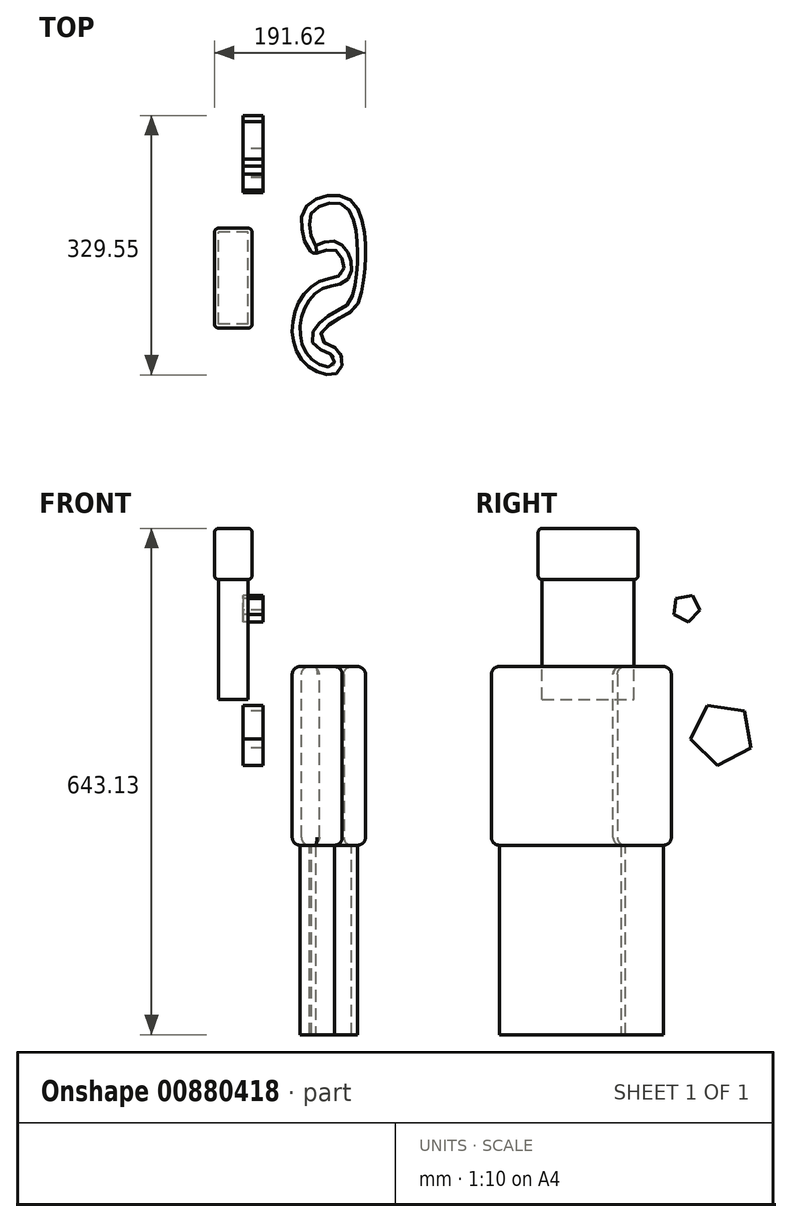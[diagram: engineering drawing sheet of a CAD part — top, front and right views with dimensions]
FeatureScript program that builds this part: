
annotation { "Feature Type Name" : "Feature", "Feature Type Description" : "" }
export const myFeature = defineFeature(function(context is Context, id is Id, definition is map)
    precondition{}
    {
        {
            var Q0;
            Q0=qCreatedBy(makeId("Front.planeOp"),FACE);
            var sketch = newSketch(context, id + "F0", { "sketchPlane" : qUnion([Q0])});
            skLineSegment(sketch, "E0.bottom", {"start": v(11.32, 23.07) * mm, "end": v(-36.3, 23.07) * mm});
            skLineSegment(sketch, "E0.top", {"start": v(11.32, -41.84) * mm, "end": v(-36.3, -41.84) * mm});
            skLineSegment(sketch, "E0.left", {"start": v(11.32, 23.07) * mm, "end": v(11.32, -41.84) * mm});
            skLineSegment(sketch, "E0.right", {"start": v(-36.3, 23.07) * mm, "end": v(-36.3, -41.84) * mm});
            skSolve(sketch);
        }
        {
            var Q0;
            Q0=qSketchRegion(id+"F0",true);
            var Q1;
            Q1=makeQuery(id+"F0.imprint","IMPRINT",FACE,{"disambiguationData":[TD([[makeQuery(id+"F0.imprint","IMPRINT",EDGE,{"derivedFrom":sQuery(id+"F0.wireOp",EDGE,"E0.bottom")}),1.0]])]});
            extrude(context, id + "F1", {"entities" : qUnion([Q0, Q1]), "depth" : 126.82 * mm, "offsetDistance" : 25 * mm});
        }
        {
            var Q0;
            Q0=makeQuery(id+"F1.opExtrude","SWEPT_FACE",FACE,{"disambiguationData":[OSD([sQuery(id+"F0.wireOp",EDGE,"E0.left")])]});
            var Q1;
            Q1=makeQuery(id+"F1.opExtrude","SWEPT_FACE",FACE,{"disambiguationData":[OSD([sQuery(id+"F0.wireOp",EDGE,"E0.right")])]});
            var Q2;
            Q2=makeQuery(id+"F1.opExtrude","CAP_FACE",FACE,{"disambiguationData":[OSD([sQuery(id+"F0.wireOp",EDGE,"E0.bottom"),sQuery(id+"F0.wireOp",EDGE,"E0.top"),sQuery(id+"F0.wireOp",EDGE,"E0.left"),sQuery(id+"F0.wireOp",EDGE,"E0.right")])],"isStart":false});
            var Q3;
            Q3=makeQuery(id+"F1.opExtrude","SWEPT_FACE",FACE,{"disambiguationData":[OSD([sQuery(id+"F0.wireOp",EDGE,"E0.bottom")])]});
            var Q4;
            Q4=makeQuery(id+"F1.opExtrude","SWEPT_FACE",FACE,{"disambiguationData":[OSD([sQuery(id+"F0.wireOp",EDGE,"E0.top")])]});
            fillet(context, id + "F2", {"entities" : qUnion([Q0, Q1, Q2, Q3, Q4]), "radius" : 5 * mm, "tangentPropagation" : true, "allowEdgeOverflow" : false});
        }
        {
            var Q0;
            Q0=makeQuery(id+"F1.opExtrude","SWEPT_FACE",FACE,{"disambiguationData":[OSD([sQuery(id+"F0.wireOp",EDGE,"E0.top")])]});
            extrude(context, id + "F3", {"entities" : qUnion([Q0]), "operationType" : NewBodyOperationType.ADD, "depth" : 110.6 * mm, "offsetDistance" : 25 * mm});
        }
        {
            var Q0;
            Q0=makeQuery(id+"F3.opExtrude","CAP_FACE",FACE,{"disambiguationData":[OSD([sQuery(id+"F0.wireOp",EDGE,"E0.top")])],"isStart":false});
            var sketch = newSketch(context, id + "F4", { "sketchPlane" : qUnion([Q0])});
            skSolve(sketch);
        }
        {
            var Q0;
            {var subQ0=sQuery(id+"F0.wireOp",EDGE,"E0.top");var subQ1=makeQuery(id+"F1.opExtrude","SWEPT_FACE",FACE,{"disambiguationData":[OSD([subQ0])]});Q0=makeQuery(id+"F4.imprint","IMPRINT",FACE,{"disambiguationData":[TD([[makeQuery(id+"F4.imprint","IMPRINT",EDGE,{"derivedFrom":makeQuery(id+"F3.opExtrude","CAP_EDGE",EDGE,{"disambiguationData":[OSD([subQ0]),TDD([makeQuery(id+"F2.opFillet","BLEND_EDGE",EDGE,{"blendedFrom":[makeQuery(id+"F1.opExtrude","CAP_EDGE",EDGE,{"disambiguationData":[OSD([subQ0])],"isStart":true}),subQ1],"blendedInto":[subQ1]})])],"isStart":false})}),1.0]])]});}
            var sketch = newSketch(context, id + "F5", { "sketchPlane" : qUnion([Q0])});
            skSolve(sketch);
        }
        {
            var Q0;
            {var subQ0=sQuery(id+"F0.wireOp",EDGE,"E0.top");var subQ1=makeQuery(id+"F1.opExtrude","SWEPT_FACE",FACE,{"disambiguationData":[OSD([subQ0])]});Q0=makeQuery(id+"F4.imprint","IMPRINT",FACE,{"disambiguationData":[TD([[makeQuery(id+"F4.imprint","IMPRINT",EDGE,{"derivedFrom":makeQuery(id+"F3.opExtrude","CAP_EDGE",EDGE,{"disambiguationData":[OSD([subQ0]),TDD([makeQuery(id+"F2.opFillet","BLEND_EDGE",EDGE,{"blendedFrom":[makeQuery(id+"F1.opExtrude","CAP_EDGE",EDGE,{"disambiguationData":[OSD([subQ0])],"isStart":true}),subQ1],"blendedInto":[subQ1]})])],"isStart":false})}),1.0]])]});}
            var sketch = newSketch(context, id + "F6", { "sketchPlane" : qUnion([Q0])});
            skSolve(sketch);
        }
        {
            var Q0;
            {var subQ0=sQuery(id+"F0.wireOp",EDGE,"E0.top");var subQ1=makeQuery(id+"F1.opExtrude","SWEPT_FACE",FACE,{"disambiguationData":[OSD([subQ0])]});Q0=makeQuery(id+"F6.imprint","IMPRINT",FACE,{"disambiguationData":[TD([[makeQuery(id+"F6.imprint","IMPRINT",EDGE,{"derivedFrom":makeQuery(id+"F4.imprint","IMPRINT",EDGE,{"derivedFrom":makeQuery(id+"F3.opExtrude","CAP_EDGE",EDGE,{"disambiguationData":[OSD([subQ0]),TDD([makeQuery(id+"F2.opFillet","BLEND_EDGE",EDGE,{"blendedFrom":[makeQuery(id+"F1.opExtrude","CAP_EDGE",EDGE,{"disambiguationData":[OSD([subQ0])],"isStart":true}),subQ1],"blendedInto":[subQ1]})])],"isStart":false})})}),1.0]])]});}
            var Q1;
            {var subQ0=sQuery(id+"F0.wireOp",EDGE,"E0.top");var subQ1=makeQuery(id+"F1.opExtrude","SWEPT_FACE",FACE,{"disambiguationData":[OSD([subQ0])]});Q1=makeQuery(id+"F4.imprint","IMPRINT",FACE,{"disambiguationData":[TD([[makeQuery(id+"F4.imprint","IMPRINT",EDGE,{"derivedFrom":makeQuery(id+"F3.opExtrude","CAP_EDGE",EDGE,{"disambiguationData":[OSD([subQ0]),TDD([makeQuery(id+"F2.opFillet","BLEND_EDGE",EDGE,{"blendedFrom":[makeQuery(id+"F1.opExtrude","CAP_EDGE",EDGE,{"disambiguationData":[OSD([subQ0])],"isStart":true}),subQ1],"blendedInto":[subQ1]})])],"isStart":false})}),1.0]])]});}
            extrude(context, id + "F7", {"entities" : qUnion([Q0, Q1]), "operationType" : NewBodyOperationType.ADD, "depth" : 41.48 * mm, "offsetDistance" : 25 * mm});
        }
        {
            var Q0;
            {var subQ0=sQuery(id+"F0.wireOp",EDGE,"E0.right");var subQ1=sQuery(id+"F0.wireOp",EDGE,"E0.top");Q0=makeQuery(id+"F7.boolean.opBoolean","MERGE",FACE,{"derivedFrom":[makeQuery(id+"F3.opExtrude","SWEPT_FACE",FACE,{"disambiguationData":[OSD([subQ1,subQ0])]}),makeQuery(id+"F7.opExtrude","SWEPT_FACE",FACE,{"disambiguationData":[OSD([subQ1,subQ0]),TDD([makeQuery(id+"F4.imprint","IMPRINT",EDGE,{"derivedFrom":makeQuery(id+"F3.opExtrude","CAP_EDGE",EDGE,{"disambiguationData":[OSD([subQ1,subQ0])],"isStart":false})})])]})]});}
            var sketch = newSketch(context, id + "F8", { "sketchPlane" : qUnion([Q0])});
            skSolve(sketch);
        }
        {
            var Q0;
            Q0=qCreatedBy(makeId("Right.planeOp"),FACE);
            var sketch = newSketch(context, id + "F9", { "sketchPlane" : qUnion([Q0])});
            skCircle(sketch, "E1.cCircle", {"center": v(61.13, -78.12) * mm, "radius": 17.9 * mm, "construction": true});
            skLineSegment(sketch, "E1.0", {"start": v(64.3, -95.74) * mm, "end": v(45.36, -86.58) * mm});
            skLineSegment(sketch, "E1.1", {"start": v(45.36, -86.58) * mm, "end": v(48.2, -65.73) * mm});
            skLineSegment(sketch, "E1.2", {"start": v(48.2, -65.73) * mm, "end": v(68.92, -62) * mm});
            skLineSegment(sketch, "E1.3", {"start": v(68.92, -62) * mm, "end": v(78.87, -80.54) * mm});
            skLineSegment(sketch, "E1.4", {"start": v(78.87, -80.54) * mm, "end": v(64.3, -95.74) * mm});
            skCircle(sketch, "E2.cCircle", {"center": v(106.86, -237.6) * mm, "radius": 40.61 * mm, "construction": true});
            skLineSegment(sketch, "E2.0", {"start": v(135.23, -208.54) * mm, "end": v(143.27, -255.6) * mm});
            skLineSegment(sketch, "E2.1", {"start": v(143.27, -255.6) * mm, "end": v(101, -277.8) * mm});
            skLineSegment(sketch, "E2.2", {"start": v(101, -277.8) * mm, "end": v(66.83, -244.45) * mm});
            skLineSegment(sketch, "E2.3", {"start": v(66.83, -244.45) * mm, "end": v(87.99, -201.65) * mm});
            skLineSegment(sketch, "E2.4", {"start": v(87.99, -201.65) * mm, "end": v(135.23, -208.54) * mm});
            skSolve(sketch);
        }
        {
            var Q0;
            Q0=makeQuery(id+"F9.imprint","IMPRINT",FACE,{"disambiguationData":[TD([[makeQuery(id+"F9.imprint","IMPRINT",EDGE,{"derivedFrom":sQuery(id+"F9.wireOp",EDGE,"E1.0")}),-1.0]])]});
            var Q1;
            Q1=makeQuery(id+"F9.imprint","IMPRINT",FACE,{"disambiguationData":[TD([[makeQuery(id+"F9.imprint","IMPRINT",EDGE,{"derivedFrom":sQuery(id+"F9.wireOp",EDGE,"E2.0")}),-1.0]])]});
            extrude(context, id + "F10", {"entities" : qUnion([Q0, Q1]), "depth" : 25 * mm, "offsetDistance" : 25 * mm});
        }
        {
            var Q0;
            {var subQ0=sQuery(id+"F0.wireOp",EDGE,"E0.right");var subQ1=sQuery(id+"F0.wireOp",EDGE,"E0.top");var subQ4=makeQuery(id+"F3.opExtrude","CAP_EDGE",EDGE,{"disambiguationData":[OSD([subQ1,subQ0])],"isStart":false});Q0=makeQuery(id+"F8.imprint","IMPRINT",FACE,{"disambiguationData":[TD([[makeQuery(id+"F8.imprint","IMPRINT",EDGE,{"derivedFrom":makeQuery(id+"F7.opExtrude","CAP_EDGE",EDGE,{"disambiguationData":[OSD([subQ1,subQ0]),TDD([makeQuery(id+"F4.imprint","IMPRINT",EDGE,{"derivedFrom":subQ4})])],"isStart":false})}),-1.0]])]});}
            var sketch = newSketch(context, id + "F11", { "sketchPlane" : qUnion([Q0])});
            skSolve(sketch);
        }
        {
            var Q0;
            {var subQ0=sQuery(id+"F0.wireOp",EDGE,"E0.top");var subQ1=makeQuery(id+"F1.opExtrude","SWEPT_FACE",FACE,{"disambiguationData":[OSD([subQ0])]});Q0=makeQuery(id+"F5.imprint","IMPRINT",FACE,{"disambiguationData":[TD([[makeQuery(id+"F5.imprint","IMPRINT",EDGE,{"derivedFrom":makeQuery(id+"F4.imprint","IMPRINT",EDGE,{"derivedFrom":makeQuery(id+"F3.opExtrude","CAP_EDGE",EDGE,{"disambiguationData":[OSD([subQ0]),TDD([makeQuery(id+"F2.opFillet","BLEND_EDGE",EDGE,{"blendedFrom":[makeQuery(id+"F1.opExtrude","CAP_EDGE",EDGE,{"disambiguationData":[OSD([subQ0])],"isStart":true}),subQ1],"blendedInto":[subQ1]})])],"isStart":false})})}),1.0]])]});}
            var sketch = newSketch(context, id + "F12", { "sketchPlane" : qUnion([Q0])});
            skFitSpline(sketch, "E3", {"points": [v(101.84, 65.35) * mm, v(66.57, 103.13) * mm, v(76.45, 169.87) * mm, v(120.42, 183.16) * mm, v(120.16, 154.64) * mm, v(97.13, 140.54) * mm, v(112.24, 120.2) * mm, v(138.37, 104.9) * mm, v(152.11, 72.2) * mm, v(138.11, -34.48) * mm, v(84.52, -31.98) * mm, v(74.57, 0) * mm, v(90.05, 31.6) * mm, v(115.92, 26.88) * mm, v(126.78, 55.75) * mm, v(101.84, 65.35) * mm]});
            skSolve(sketch);
        }
        {
            var Q0;
            Q0 = qSketchRegion(id + "F12", true);
            var Q1;
            Q1=makeQuery(id+"F12.imprint","IMPRINT",FACE,{"disambiguationData":[TD([[makeQuery(id+"F12.imprint","IMPRINT",EDGE,{"derivedFrom":sQuery(id+"F12.wireOp",EDGE,"E3")}),-1.0]])]});
            extrude(context, id + "F13", {"entities" : qUnion([Q0, Q1]), "depth" : 226.98 * mm, "offsetDistance" : 25 * mm});
        }
        {
            var Q0;
            Q0=makeQuery(id+"F13.opExtrude","CAP_EDGE",EDGE,{"disambiguationData":[OSD([sQuery(id+"F12.wireOp",EDGE,"E3")])],"isStart":true});
            var Q1;
            Q1=makeQuery(id+"F13.opExtrude","CAP_EDGE",EDGE,{"disambiguationData":[OSD([sQuery(id+"F12.wireOp",EDGE,"E3")])],"isStart":false});
            fillet(context, id + "F14", {"entities" : qUnion([Q0, Q1]), "radius" : 10 * mm, "tangentPropagation" : true, "allowEdgeOverflow" : false});
        }
        {
            var Q0;
            Q0=makeQuery(id+"F13.opExtrude","CAP_FACE",FACE,{"disambiguationData":[OSD([sQuery(id+"F12.wireOp",EDGE,"E3")])],"isStart":false});
            extrude(context, id + "F15", {"entities" : qUnion([Q0]), "operationType" : NewBodyOperationType.ADD, "depth" : 240.65 * mm, "offsetDistance" : 25 * mm});
        }
    });
